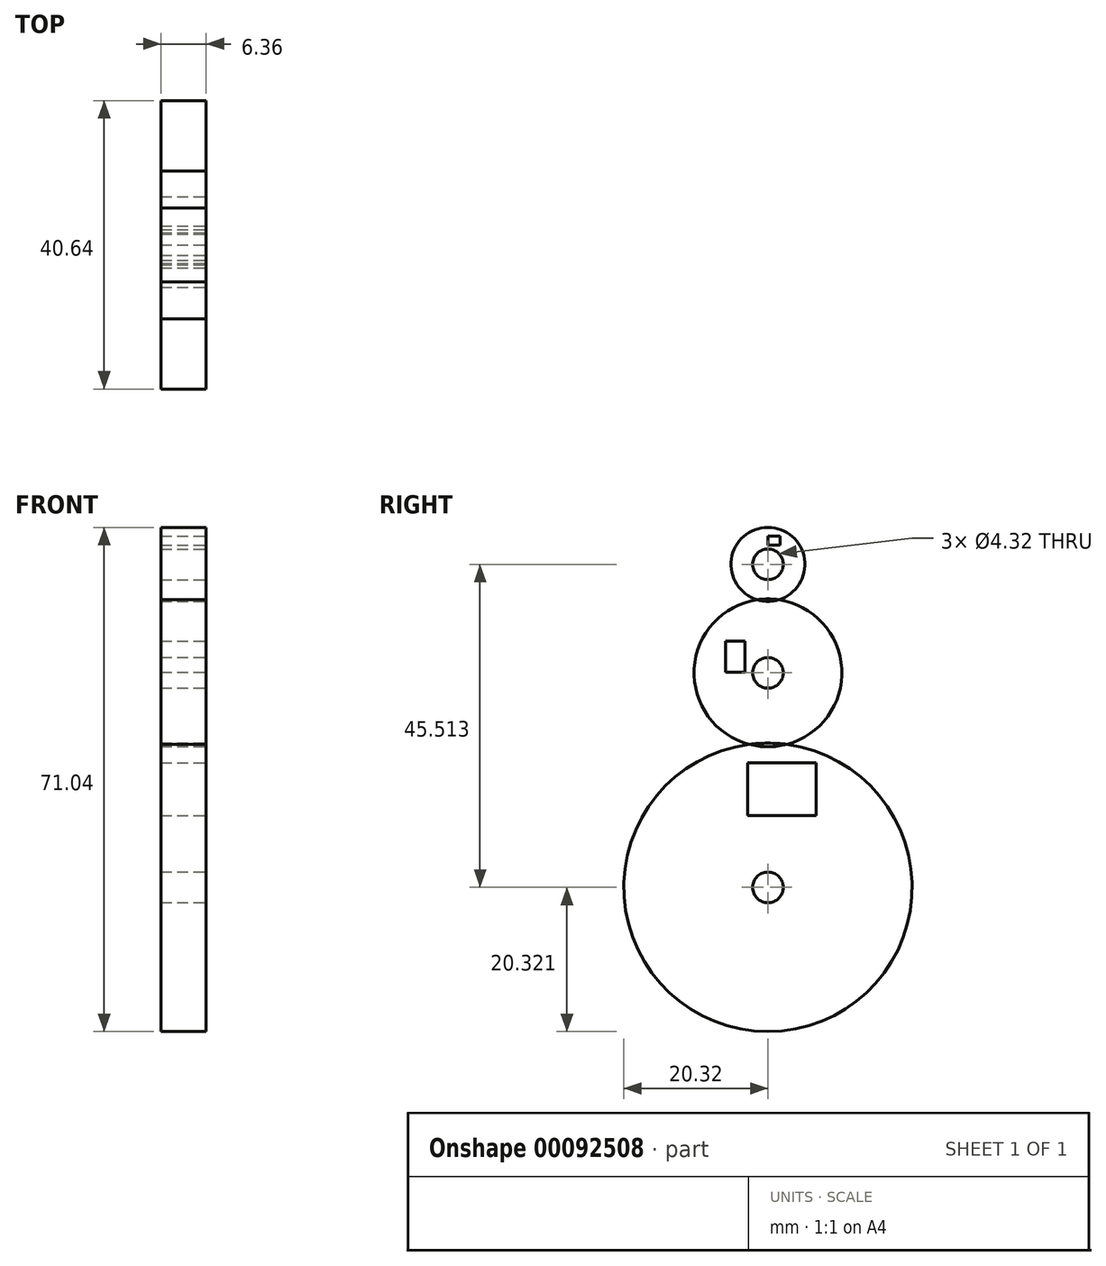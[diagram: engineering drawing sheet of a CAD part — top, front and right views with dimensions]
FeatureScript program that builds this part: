
annotation { "Feature Type Name" : "Feature", "Feature Type Description" : "" }
export const myFeature = defineFeature(function(context is Context, id is Id, definition is map)
    precondition{}
    {
        {
            var Q0;
            Q0=qCreatedBy(makeId("Right.planeOp"),FACE);
            var sketch = newSketch(context, id + "F0", { "sketchPlane" : qUnion([Q0])});
            skCircle(sketch, "E0", {"center": v(0, 9.96) * mm, "radius": 2.16 * mm});
            skCircle(sketch, "E1", {"center": v(0, -5.33) * mm, "radius": 10.41 * mm});
            skLineSegment(sketch, "E2.bottom", {"start": v(-24.7, 17.52) * mm, "end": v(24.7, 17.52) * mm});
            skLineSegment(sketch, "E2.top", {"start": v(-24.7, -61.35) * mm, "end": v(24.7, -61.35) * mm});
            skLineSegment(sketch, "E2.left", {"start": v(-24.7, 17.52) * mm, "end": v(-24.7, -61.35) * mm});
            skLineSegment(sketch, "E2.right", {"start": v(24.7, 17.52) * mm, "end": v(24.7, -61.35) * mm});
            skCircle(sketch, "E3", {"center": v(0, -5.33) * mm, "radius": 2.16 * mm});
            skCircle(sketch, "E4", {"center": v(0, 9.96) * mm, "radius": 5.2 * mm});
            skCircle(sketch, "E5", {"center": v(0, -35.55) * mm, "radius": 2.16 * mm});
            skCircle(sketch, "E6", {"center": v(0, -35.55) * mm, "radius": 20.32 * mm});
            skLineSegment(sketch, "E7.bottom", {"start": v(-5.97, -0.83) * mm, "end": v(-3.27, -0.83) * mm});
            skLineSegment(sketch, "E7.top", {"start": v(-5.97, -5.25) * mm, "end": v(-3.27, -5.25) * mm});
            skLineSegment(sketch, "E7.left", {"start": v(-5.97, -0.83) * mm, "end": v(-5.97, -5.25) * mm});
            skLineSegment(sketch, "E7.right", {"start": v(-3.27, -0.83) * mm, "end": v(-3.27, -5.25) * mm});
            skLineSegment(sketch, "E8.bottom", {"start": v(0, 13.95) * mm, "end": v(1.7, 13.95) * mm});
            skLineSegment(sketch, "E8.top", {"start": v(0, 12.66) * mm, "end": v(1.7, 12.66) * mm});
            skLineSegment(sketch, "E8.left", {"start": v(0, 13.95) * mm, "end": v(0, 12.66) * mm});
            skLineSegment(sketch, "E8.right", {"start": v(1.7, 13.95) * mm, "end": v(1.7, 12.66) * mm});
            skLineSegment(sketch, "E9.bottom", {"start": v(-2.84, -17.98) * mm, "end": v(6.76, -17.98) * mm});
            skLineSegment(sketch, "E9.top", {"start": v(-2.84, -25.42) * mm, "end": v(6.76, -25.42) * mm});
            skLineSegment(sketch, "E9.left", {"start": v(-2.84, -17.98) * mm, "end": v(-2.84, -25.42) * mm});
            skLineSegment(sketch, "E9.right", {"start": v(6.76, -17.98) * mm, "end": v(6.76, -25.42) * mm});
            skSolve(sketch);
        }
        {
            var Q0;
            Q0=makeQuery(id+"F0.imprint","IMPRINT",FACE,{"disambiguationData":[TD([[makeQuery(id+"F0.imprint","IMPRINT",EDGE,{"derivedFrom":sQuery(id+"F0.wireOp",EDGE,"E0")}),-1.0]])]});
            var Q1;
            Q1=makeQuery(id+"F0.imprint","IMPRINT",FACE,{"disambiguationData":[TD([[makeQuery(id+"F0.imprint","IMPRINT",EDGE,{"derivedFrom":sQuery(id+"F0.wireOp",EDGE,"E3")}),-1.0]])]});
            var Q2;
            Q2=makeQuery(id+"F0.imprint","IMPRINT",FACE,{"disambiguationData":[TD([[makeQuery(id+"F0.imprint","IMPRINT",EDGE,{"derivedFrom":sQuery(id+"F0.wireOp",EDGE,"E5")}),-1.0]])]});
            extrude(context, id + "F1", {"entities" : qUnion([Q0, Q1, Q2]), "endBound" : BoundingType.SYMMETRIC, "oppositeDirection" : true, "depth" : 6.35 * mm});
        }
    });
